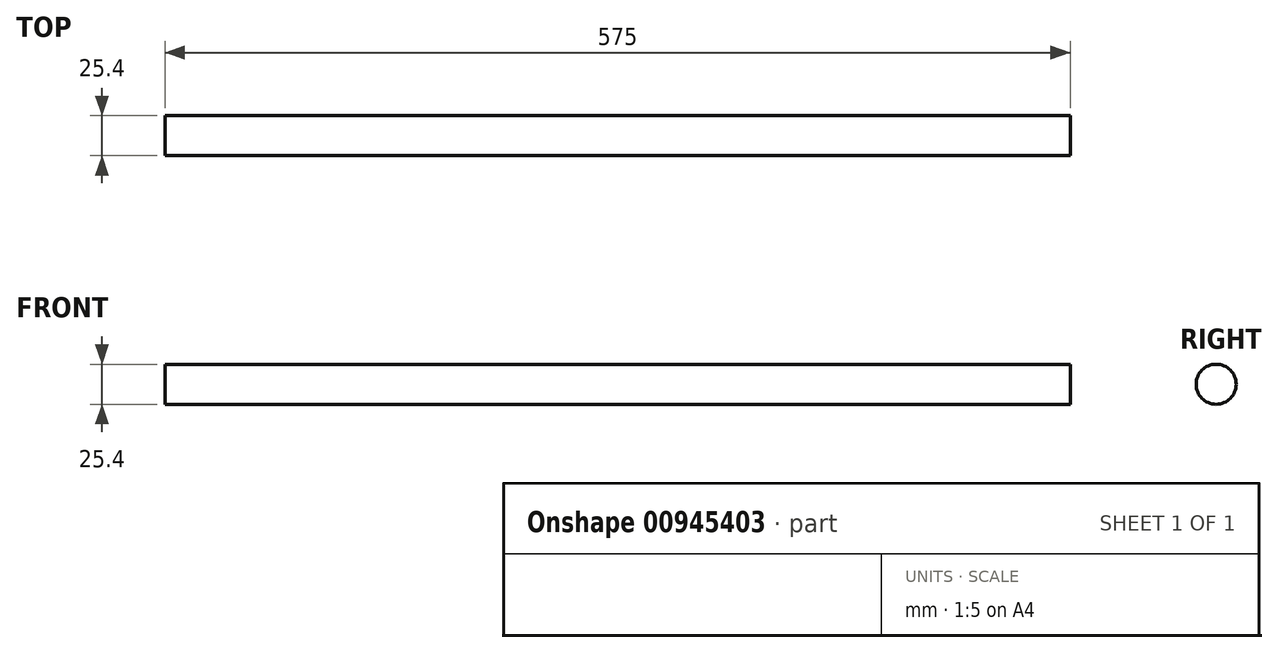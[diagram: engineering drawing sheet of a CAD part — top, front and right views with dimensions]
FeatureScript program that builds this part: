
annotation { "Feature Type Name" : "Feature", "Feature Type Description" : "" }
export const myFeature = defineFeature(function(context is Context, id is Id, definition is map)
    precondition{}
    {
        {
            var Q0;
            Q0=qCreatedBy(makeId("Right.planeOp"),FACE);
            var sketch = newSketch(context, id + "F0", { "sketchPlane" : qUnion([Q0])});
            skCircle(sketch, "E0", {"center": v(0, 0) * mm, "radius": 12.7 * mm});
            skSolve(sketch);
        }
        {
            var Q0;
            Q0=sQuery(id+"F0.wireOp",EDGE,"E0");
            extrude(context, id + "F1", {"bodyType" : ToolBodyType.SURFACE, "surfaceEntities" : qUnion([Q0]), "depth" : 575 * mm, "offsetDistance" : 25.4 * mm});
        }
    });
